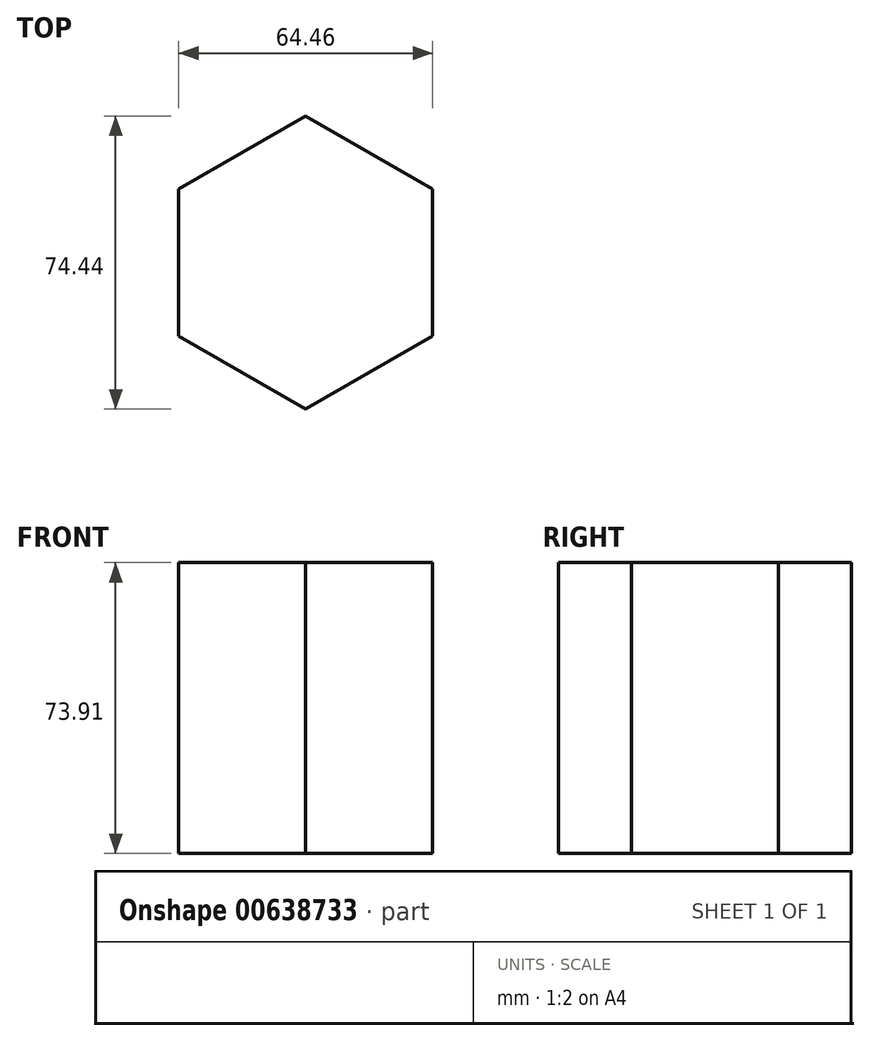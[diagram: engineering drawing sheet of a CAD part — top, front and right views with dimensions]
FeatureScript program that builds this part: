
annotation { "Feature Type Name" : "Feature", "Feature Type Description" : "" }
export const myFeature = defineFeature(function(context is Context, id is Id, definition is map)
    precondition{}
    {
        {
            var Q0;
            Q0=qCreatedBy(makeId("Top.planeOp"),FACE);
            var sketch = newSketch(context, id + "F0", { "sketchPlane" : qUnion([Q0])});
            skCircle(sketch, "E0.cCircle", {"center": v(0, 0) * mm, "radius": 32.23 * mm, "construction": true});
            skLineSegment(sketch, "E0.0", {"start": v(32.23, 18.6) * mm, "end": v(32.23, -18.6) * mm});
            skLineSegment(sketch, "E0.1", {"start": v(32.23, -18.6) * mm, "end": v(0, -37.22) * mm});
            skLineSegment(sketch, "E0.2", {"start": v(0, -37.22) * mm, "end": v(-32.23, -18.6) * mm});
            skLineSegment(sketch, "E0.3", {"start": v(-32.23, -18.6) * mm, "end": v(-32.23, 18.6) * mm});
            skLineSegment(sketch, "E0.4", {"start": v(-32.23, 18.6) * mm, "end": v(0, 37.22) * mm});
            skLineSegment(sketch, "E0.5", {"start": v(0, 37.22) * mm, "end": v(32.23, 18.6) * mm});
            skPoint(sketch, "E0.0.midPoint", {"position": v(32.23, 0) * mm});
            skSolve(sketch);
        }
        {
            var Q0;
            Q0=makeQuery(id+"F0.imprint","IMPRINT",FACE,{"disambiguationData":[TD([[makeQuery(id+"F0.imprint","IMPRINT",EDGE,{"derivedFrom":sQuery(id+"F0.wireOp",EDGE,"E0.0")}),-1.0]])]});
            extrude(context, id + "F1", {"entities" : qUnion([Q0]), "depth" : 73.9 * mm, "offsetDistance" : 25.4 * mm});
        }
    });
